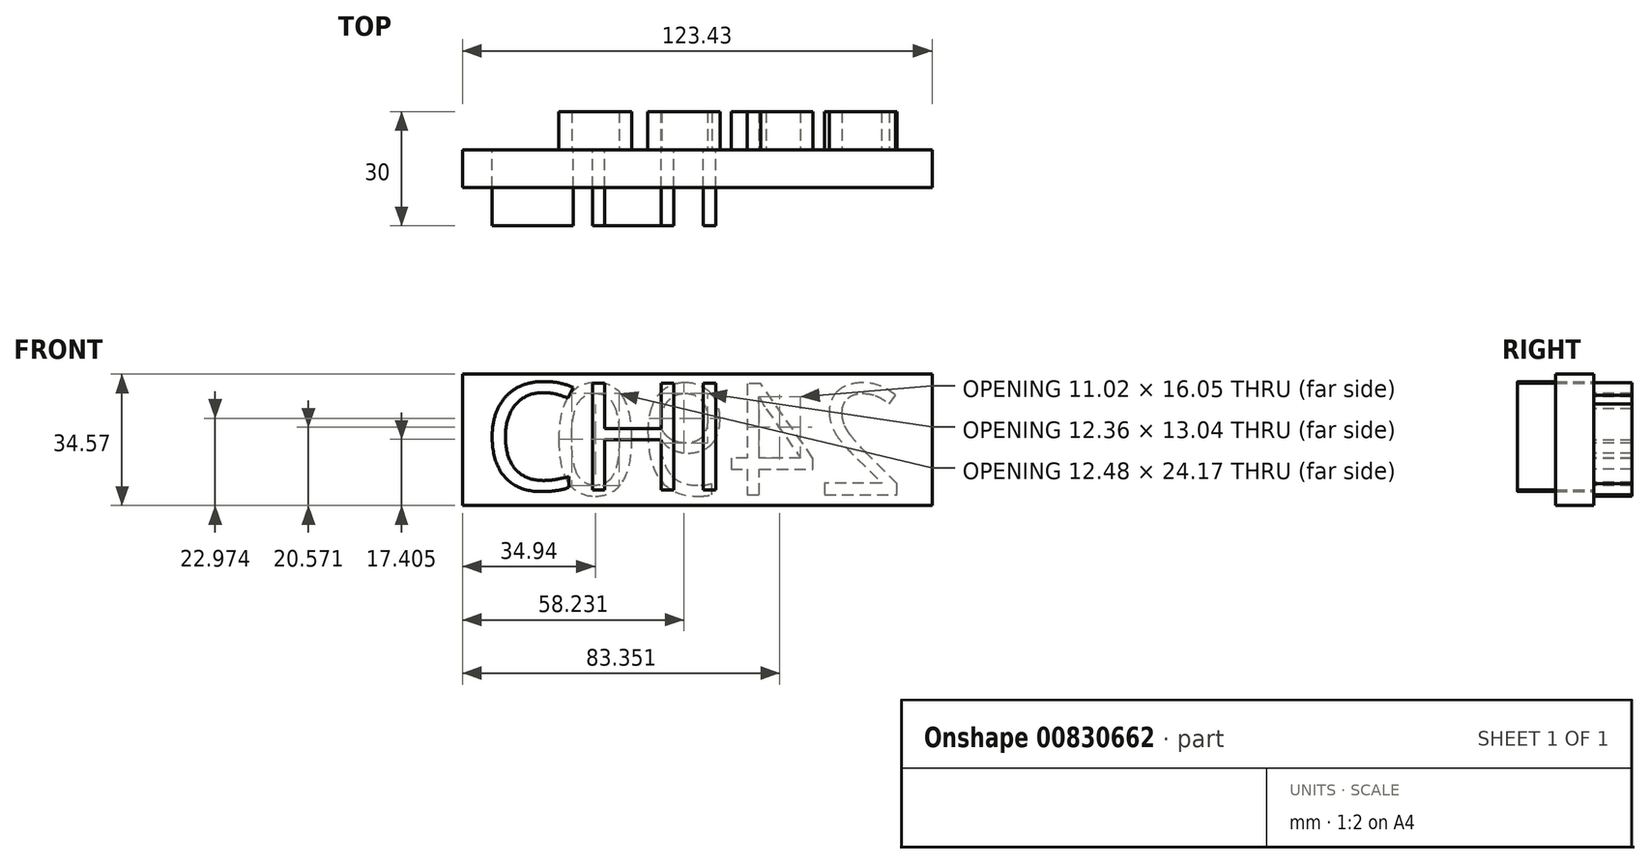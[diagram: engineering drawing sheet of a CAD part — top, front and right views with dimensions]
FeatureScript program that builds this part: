
annotation { "Feature Type Name" : "Feature", "Feature Type Description" : "" }
export const myFeature = defineFeature(function(context is Context, id is Id, definition is map)
    precondition{}
    {
        {
            var Q0;
            Q0=qCreatedBy(makeId("Front.planeOp"),FACE);
            var sketch = newSketch(context, id + "F0", { "sketchPlane" : qUnion([Q0])});
            skLineSegment(sketch, "E0.bottom", {"start": v(0, 0) * mm, "end": v(123.43, 0) * mm});
            skLineSegment(sketch, "E0.top", {"start": v(0, 34.57) * mm, "end": v(123.43, 34.57) * mm});
            skLineSegment(sketch, "E0.left", {"start": v(0, 0) * mm, "end": v(0, 34.57) * mm});
            skLineSegment(sketch, "E0.right", {"start": v(123.43, 0) * mm, "end": v(123.43, 34.57) * mm});
            skSolve(sketch);
        }
        {
            var Q0;
            Q0=makeQuery(id+"F0.imprint","IMPRINT",FACE,{"disambiguationData":[TD([[makeQuery(id+"F0.imprint","IMPRINT",EDGE,{"derivedFrom":sQuery(id+"F0.wireOp",EDGE,"E0.bottom")}),1.0]])]});
            var sketch = newSketch(context, id + "F1", { "sketchPlane" : qUnion([Q0])});
            skText(sketch, "E1", { "text": "CHI", "fontName": "OpenSans-Regular.ttf"});
            const initialGuessF1  = {"E1": [0.0054, 0.00407, 1, 0, 0.0284]};
            skSetInitialGuess(sketch, initialGuessF1);
            skSolve(sketch);
        }
        {
            var Q0;
            Q0 = qSketchRegion(id + "F1", true);
            extrude(context, id + "F2", {"entities" : qUnion([Q0]), "depth" : 20 * mm, "offsetDistance" : 25.4 * mm});
        }
        {
            var Q0;
            Q0 = qSketchRegion(id + "F0", true);
            extrude(context, id + "F3", {"entities" : qUnion([Q0]), "depth" : 10 * mm, "offsetDistance" : 25.4 * mm});
        }
        {
            var Q0;
            Q0=makeQuery(id+"F3.opExtrude","CAP_FACE",FACE,{"disambiguationData":[OSD([sQuery(id+"F0.wireOp",EDGE,"E0.bottom"),sQuery(id+"F0.wireOp",EDGE,"E0.top"),sQuery(id+"F0.wireOp",EDGE,"E0.left"),sQuery(id+"F0.wireOp",EDGE,"E0.right")])],"isStart":true});
            var sketch = newSketch(context, id + "F4", { "sketchPlane" : qUnion([Q0])});
            skText(sketch, "E2", { "text": "2490", "fontName": "OpenSans-Regular.ttf"});
            const initialGuessF4  = {"E2": [-0.11624, 0.00288, 1, 0, 0.02926]};
            skSetInitialGuess(sketch, initialGuessF4);
            skSolve(sketch);
        }
        {
            var Q0;
            Q0 = qSketchRegion(id + "F4", true);
            extrude(context, id + "F5", {"entities" : qUnion([Q0]), "depth" : 10 * mm, "offsetDistance" : 25.4 * mm});
        }
    });
